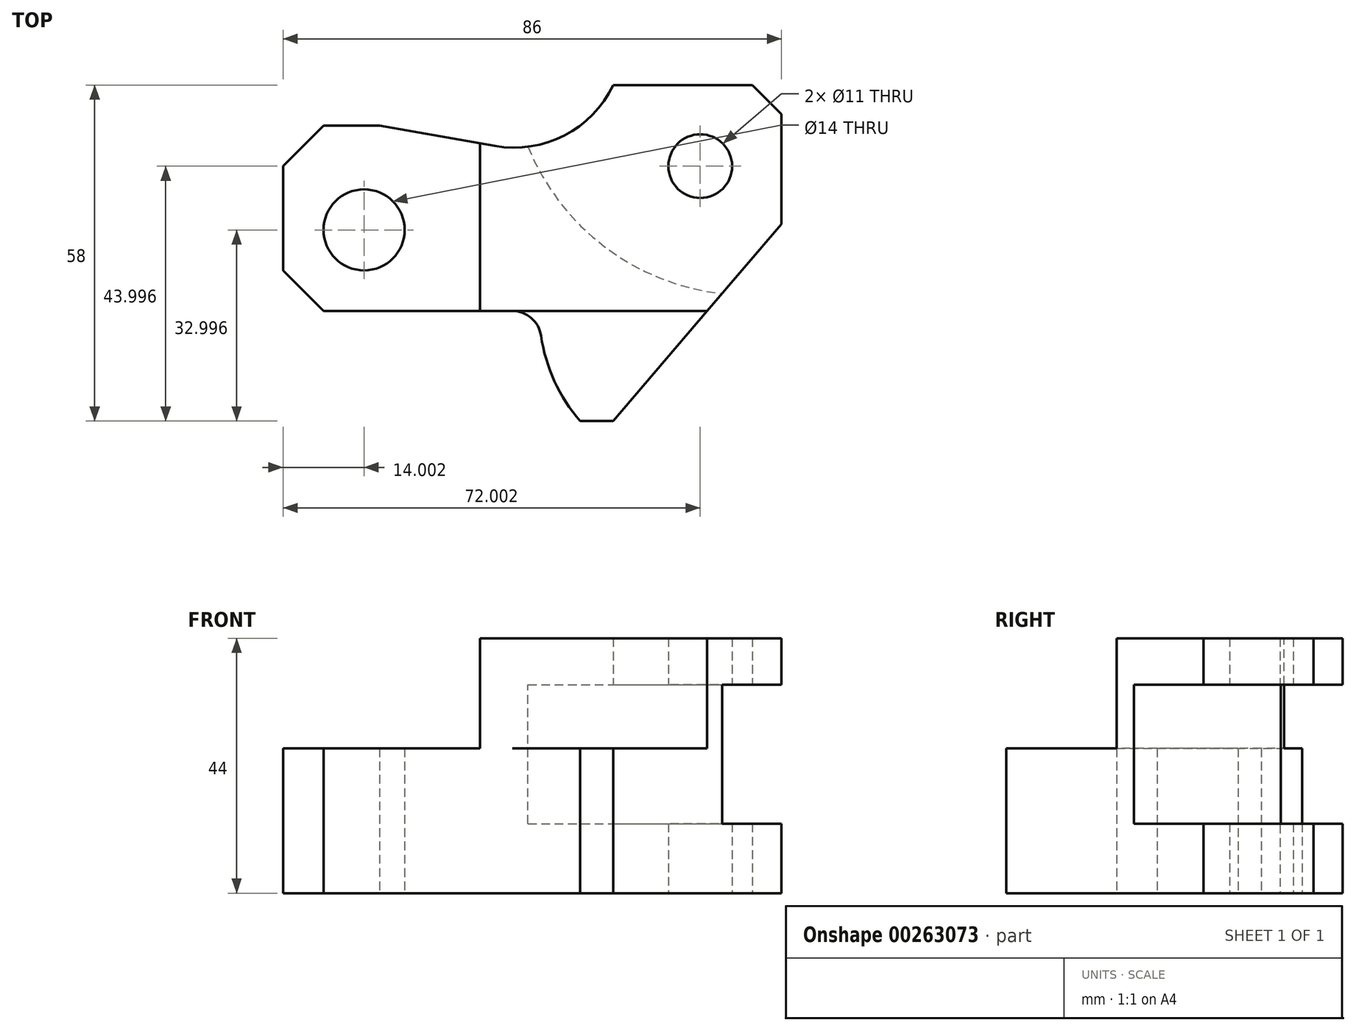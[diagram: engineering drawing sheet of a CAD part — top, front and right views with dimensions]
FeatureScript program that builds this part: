
annotation { "Feature Type Name" : "Feature", "Feature Type Description" : "" }
export const myFeature = defineFeature(function(context is Context, id is Id, definition is map)
    precondition{}
    {
        {
            var Q0;
            Q0=qCreatedBy(makeId("Top.planeOp"),FACE);
            var sketch = newSketch(context, id + "F0", { "sketchPlane" : qUnion([Q0])});
            skLineSegment(sketch, "E0", {"start": v(-30.09, 16.77) * mm, "end": v(-37.09, 9.77) * mm});
            skLineSegment(sketch, "E1", {"start": v(-37.09, 9.77) * mm, "end": v(-37.09, -8.23) * mm});
            skLineSegment(sketch, "E2", {"start": v(-37.09, -8.23) * mm, "end": v(-30.09, -15.23) * mm});
            skLineSegment(sketch, "E3", {"start": v(19.91, 23.77) * mm, "end": v(43.91, 23.77) * mm});
            skLineSegment(sketch, "E4", {"start": v(43.91, 23.77) * mm, "end": v(48.91, 18.77) * mm});
            skLineSegment(sketch, "E5", {"start": v(48.91, 18.77) * mm, "end": v(48.91, -0.23) * mm});
            skLineSegment(sketch, "E6", {"start": v(-30.09, -15.23) * mm, "end": v(2.49, -15.23) * mm});
            skPoint(sketch, "E7.visualSharp", {"position": v(20.83, -15.23) * mm});
            skLineSegment(sketch, "E8", {"start": v(19.91, -34.23) * mm, "end": v(14.2, -34.23) * mm});
            skLineSegment(sketch, "E9", {"start": v(19.91, -34.23) * mm, "end": v(48.91, -0.23) * mm});
            skCircle(sketch, "E10", {"center": v(-23.09, -1.23) * mm, "radius": 7 * mm});
            skLineSegment(sketch, "E11", {"start": v(-37.09, 9.77) * mm, "end": v(-37.09, 44.31) * mm, "construction": true});
            skLineSegment(sketch, "E12", {"start": v(-37.09, -8.23) * mm, "end": v(-37.09, -23.05) * mm, "construction": true});
            skLineSegment(sketch, "E13", {"start": v(48.91, 18.77) * mm, "end": v(48.91, 37.84) * mm, "construction": true});
            skLineSegment(sketch, "E14", {"start": v(-30.09, 16.77) * mm, "end": v(-20.45, 16.77) * mm});
            skLineSegment(sketch, "E15", {"start": v(-20.45, 16.77) * mm, "end": v(-0.53, 13.25) * mm});
            skPoint(sketch, "E16.visualSharp", {"position": v(4.9, -15.23) * mm});
            skArc(sketch, "E16.filletArc", {"start": v(7.43, -19.5) * mm, "mid": v(5.75, -16.45) * mm, "end": v(2.49, -15.23) * mm});
            skPoint(sketch, "E17", {"position": v(36.12, -15.23) * mm});
            skArc(sketch, "E18", {"start": v(7.43, -19.5) * mm, "mid": v(9.77, -27.35) * mm, "end": v(14.2, -34.23) * mm});
            skLineSegment(sketch, "E19", {"start": v(-20.45, 16.77) * mm, "end": v(-4.48, 16.77) * mm, "construction": true});
            skArc(sketch, "E20", {"start": v(-0.53, 13.25) * mm, "mid": v(11.46, 15.07) * mm, "end": v(19.91, 23.77) * mm});
            skCircle(sketch, "E21", {"center": v(34.91, 9.77) * mm, "radius": 5.5 * mm});
            skLineSegment(sketch, "E22", {"start": v(-3.09, -15.23) * mm, "end": v(-3.09, 13.7) * mm, "construction": true});
            skSolve(sketch);
        }
        {
            var Q0;
            Q0 = qSketchRegion(id + "F0", true);
            extrude(context, id + "F1", {"entities" : qUnion([Q0]), "depth" : 44 * mm});
        }
        {
            var Q0;
            Q0=makeQuery(id+"F1.opExtrude","CAP_FACE",FACE,{"disambiguationData":[OSD([sQuery(id+"F0.wireOp",EDGE,"E0"),sQuery(id+"F0.wireOp",EDGE,"E1"),sQuery(id+"F0.wireOp",EDGE,"E2"),sQuery(id+"F0.wireOp",EDGE,"E3"),sQuery(id+"F0.wireOp",EDGE,"E4"),sQuery(id+"F0.wireOp",EDGE,"E5"),sQuery(id+"F0.wireOp",EDGE,"E6"),sQuery(id+"F0.wireOp",EDGE,"E8"),sQuery(id+"F0.wireOp",EDGE,"E9"),sQuery(id+"F0.wireOp",EDGE,"E10"),sQuery(id+"F0.wireOp",EDGE,"E14"),sQuery(id+"F0.wireOp",EDGE,"E15"),sQuery(id+"F0.wireOp",EDGE,"E16.filletArc"),sQuery(id+"F0.wireOp",EDGE,"E18"),sQuery(id+"F0.wireOp",EDGE,"E20"),sQuery(id+"F0.wireOp",EDGE,"E21")])],"isStart":false});
            var sketch = newSketch(context, id + "F2", { "sketchPlane" : qUnion([Q0])});
            skLineSegment(sketch, "E23", {"start": v(-3.09, -15.23) * mm, "end": v(-3.09, 13.7) * mm});
            skSolve(sketch);
        }
        {
            var Q0;
            {var subQ1=sQuery(id+"F2.wireOp",EDGE,"E23");Q0=makeQuery(id+"F2.imprint","IMPRINT",FACE,{"disambiguationData":[TD([[makeQuery(id+"F2.imprint","IMPRINT",EDGE,{"derivedFrom":subQ1}),1.0]])]});}
            extrude(context, id + "F3", {"entities" : qUnion([Q0]), "operationType" : NewBodyOperationType.REMOVE, "oppositeDirection" : true, "depth" : 19 * mm});
        }
        {
            var Q0;
            Q0=makeQuery(id+"F1.opExtrude","CAP_FACE",FACE,{"disambiguationData":[OSD([sQuery(id+"F0.wireOp",EDGE,"E0"),sQuery(id+"F0.wireOp",EDGE,"E1"),sQuery(id+"F0.wireOp",EDGE,"E2"),sQuery(id+"F0.wireOp",EDGE,"E3"),sQuery(id+"F0.wireOp",EDGE,"E4"),sQuery(id+"F0.wireOp",EDGE,"E5"),sQuery(id+"F0.wireOp",EDGE,"E6"),sQuery(id+"F0.wireOp",EDGE,"E8"),sQuery(id+"F0.wireOp",EDGE,"E9"),sQuery(id+"F0.wireOp",EDGE,"E10"),sQuery(id+"F0.wireOp",EDGE,"E14"),sQuery(id+"F0.wireOp",EDGE,"E15"),sQuery(id+"F0.wireOp",EDGE,"E16.filletArc"),sQuery(id+"F0.wireOp",EDGE,"E18"),sQuery(id+"F0.wireOp",EDGE,"E20"),sQuery(id+"F0.wireOp",EDGE,"E21")])],"isStart":false});
            cPlane(context, id + "F4", {"entities" : qUnion([Q0]), "cplaneType" : CPlaneType.OFFSET, "offset" : 8 * mm, "oppositeDirection" : true, "width" : 150 * mm, "height" : 150 * mm});
        }
        {
            var Q0;
            Q0=qCreatedBy(id+"F4.planeOp",FACE);
            var sketch = newSketch(context, id + "F5", { "sketchPlane" : qUnion([Q0])});
            skPoint(sketch, "E24", {"position": v(38.68, -12.23) * mm});
            skCircle(sketch, "E25", {"center": v(43.19, 28.52) * mm, "radius": 41 * mm});
            skPoint(sketch, "E26.0.10.end.orphan", {"position": v(-3.09, 13.7) * mm});
            skPoint(sketch, "E26.0.10.start.orphan", {"position": v(-0.53, 13.25) * mm});
            skPoint(sketch, "E26.0.1.start.orphan", {"position": v(-3.09, -15.23) * mm});
            skPoint(sketch, "E26.0.2.start.orphan", {"position": v(2.49, -15.23) * mm});
            skPoint(sketch, "E26.0.3.start.orphan", {"position": v(7.43, -19.5) * mm});
            skPoint(sketch, "E26.0.4.start.orphan", {"position": v(14.2, -34.23) * mm});
            skPoint(sketch, "E27.orphan", {"position": v(19.91, -34.23) * mm});
            skPoint(sketch, "E26.0.8.end.orphan", {"position": v(19.91, 23.77) * mm});
            skPoint(sketch, "E26.0.7.end.orphan", {"position": v(43.91, 23.77) * mm});
            skPoint(sketch, "E26.0.6.end.orphan", {"position": v(48.91, 18.77) * mm});
            skPoint(sketch, "E26.0.5.end.orphan", {"position": v(48.91, -0.23) * mm});
            skSolve(sketch);
        }
        {
            var Q0;
            Q0=makeQuery(id+"F5.imprint","IMPRINT",FACE,{"disambiguationData":[TD([[makeQuery(id+"F5.imprint","IMPRINT",EDGE,{"derivedFrom":sQuery(id+"F5.wireOp",EDGE,"E25")}),1.0]])]});
            var Q1;
            Q1=sQuery(id+"F5.wireOp",EDGE,"E25");
            extrude(context, id + "F6", {"entities" : qUnion([Q0]), "operationType" : NewBodyOperationType.REMOVE, "surfaceEntities" : qUnion([Q1]), "oppositeDirection" : true, "depth" : 24 * mm});
        }
        {
            var Q0;
            Q0=makeQuery(id+"F1.opExtrude","CAP_FACE",FACE,{"disambiguationData":[OSD([sQuery(id+"F0.wireOp",EDGE,"E0"),sQuery(id+"F0.wireOp",EDGE,"E1"),sQuery(id+"F0.wireOp",EDGE,"E2"),sQuery(id+"F0.wireOp",EDGE,"E3"),sQuery(id+"F0.wireOp",EDGE,"E4"),sQuery(id+"F0.wireOp",EDGE,"E5"),sQuery(id+"F0.wireOp",EDGE,"E6"),sQuery(id+"F0.wireOp",EDGE,"E8"),sQuery(id+"F0.wireOp",EDGE,"E9"),sQuery(id+"F0.wireOp",EDGE,"E10"),sQuery(id+"F0.wireOp",EDGE,"E14"),sQuery(id+"F0.wireOp",EDGE,"E15"),sQuery(id+"F0.wireOp",EDGE,"E16.filletArc"),sQuery(id+"F0.wireOp",EDGE,"E18"),sQuery(id+"F0.wireOp",EDGE,"E20"),sQuery(id+"F0.wireOp",EDGE,"E21")])],"isStart":false});
            var sketch = newSketch(context, id + "F7", { "sketchPlane" : qUnion([Q0])});
            skPoint(sketch, "E28", {"position": v(34.41, -17.23) * mm});
            skLineSegment(sketch, "E29.0.1", {"start": v(-3.09, -15.23) * mm, "end": v(2.49, -15.23) * mm});
            skArc(sketch, "E29.0.2", {"start": v(2.49, -15.23) * mm, "mid": v(5.75, -16.45) * mm, "end": v(7.43, -19.5) * mm});
            skArc(sketch, "E29.0.3", {"start": v(7.43, -19.5) * mm, "mid": v(9.77, -27.35) * mm, "end": v(14.2, -34.23) * mm});
            skLineSegment(sketch, "E29.0.4", {"start": v(14.2, -34.23) * mm, "end": v(19.91, -34.23) * mm});
            skLineSegment(sketch, "E29.0.5", {"start": v(19.91, -34.23) * mm, "end": v(36.12, -15.23) * mm});
            skLineSegment(sketch, "E29.0.6", {"start": v(48.91, -0.23) * mm, "end": v(48.91, 18.77) * mm});
            skLineSegment(sketch, "E29.0.7", {"start": v(48.91, 18.77) * mm, "end": v(43.91, 23.77) * mm});
            skLineSegment(sketch, "E29.0.8", {"start": v(43.91, 23.77) * mm, "end": v(19.91, 23.77) * mm});
            skArc(sketch, "E29.0.9", {"start": v(19.91, 23.77) * mm, "mid": v(11.46, 15.07) * mm, "end": v(-0.53, 13.25) * mm});
            skLineSegment(sketch, "E29.0.10", {"start": v(-0.53, 13.25) * mm, "end": v(-3.09, 13.7) * mm});
            skLineSegment(sketch, "E30", {"start": v(36.12, -15.23) * mm, "end": v(2.49, -15.23) * mm});
            skSolve(sketch);
        }
        {
            var Q0;
            Q0=makeQuery(id+"F7.imprint","IMPRINT",FACE,{"disambiguationData":[TD([[makeQuery(id+"F7.imprint","IMPRINT",EDGE,{"derivedFrom":sQuery(id+"F7.wireOp",EDGE,"E29.0.2")}),-1.0]])]});
            extrude(context, id + "F8", {"entities" : qUnion([Q0]), "operationType" : NewBodyOperationType.REMOVE, "oppositeDirection" : true, "depth" : 19 * mm});
        }
    });
